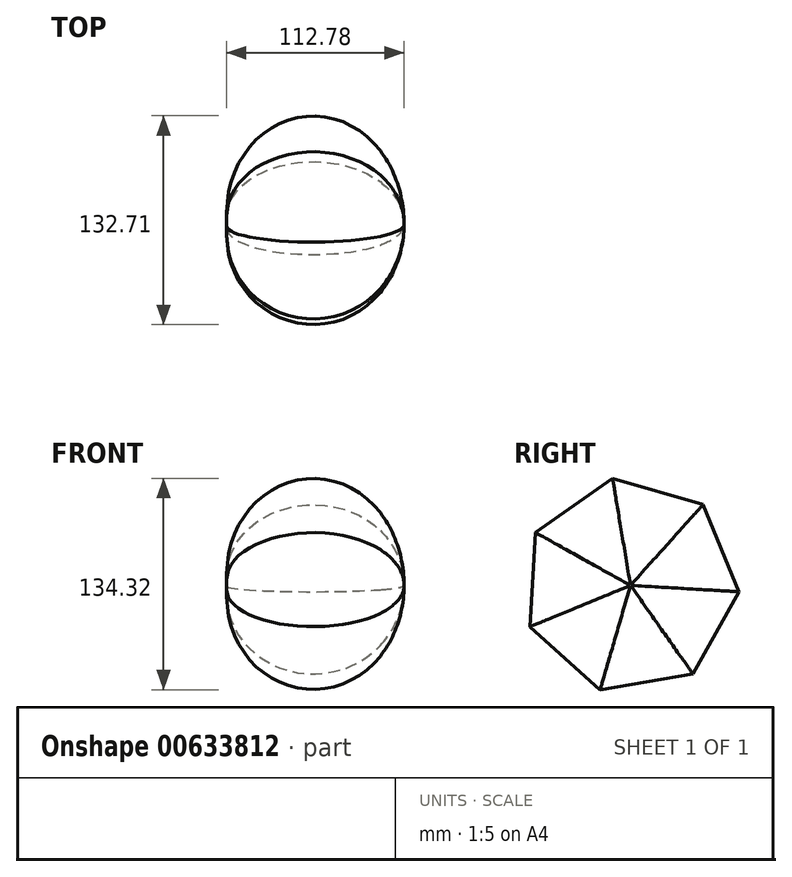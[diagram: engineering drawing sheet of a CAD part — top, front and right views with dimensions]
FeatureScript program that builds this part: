
annotation { "Feature Type Name" : "Feature", "Feature Type Description" : "" }
export const myFeature = defineFeature(function(context is Context, id is Id, definition is map)
    precondition{}
    {
        {
            var Q0;
            Q0=qCreatedBy(makeId("Right.planeOp"),FACE);
            var sketch = newSketch(context, id + "F0", { "sketchPlane" : qUnion([Q0])});
            skCircle(sketch, "E0", {"center": v(-0.1, 0.47) * mm, "radius": 76.2 * mm});
            skSolve(sketch);
        }
        {
            var Q0;
            Q0=makeQuery(id+"F0.imprint","IMPRINT",FACE,{"disambiguationData":[TD([[makeQuery(id+"F0.imprint","IMPRINT",EDGE,{"derivedFrom":sQuery(id+"F0.wireOp",EDGE,"E0")}),1.0]])]});
            var sketch = newSketch(context, id + "F1", { "sketchPlane" : qUnion([Q0])});
            skCircle(sketch, "E1.cCircle", {"center": v(0, 0) * mm, "radius": 65.95 * mm, "construction": true});
            skLineSegment(sketch, "E1.0", {"start": v(73.07, -4.29) * mm, "end": v(42.2, -59.8) * mm});
            skLineSegment(sketch, "E1.1", {"start": v(42.2, -59.8) * mm, "end": v(-20.44, -70.28) * mm});
            skLineSegment(sketch, "E1.2", {"start": v(-20.44, -70.28) * mm, "end": v(-67.7, -27.84) * mm});
            skLineSegment(sketch, "E1.3", {"start": v(-67.7, -27.84) * mm, "end": v(-63.97, 35.56) * mm});
            skLineSegment(sketch, "E1.4", {"start": v(-63.97, 35.56) * mm, "end": v(-12.08, 72.19) * mm});
            skLineSegment(sketch, "E1.5", {"start": v(-12.08, 72.19) * mm, "end": v(48.9, 54.46) * mm});
            skLineSegment(sketch, "E1.6", {"start": v(48.9, 54.46) * mm, "end": v(73.07, -4.29) * mm});
            skPoint(sketch, "E1.0.midPoint", {"position": v(57.64, -32.04) * mm});
            skSolve(sketch);
        }
        {
            var Q0;
            Q0 = qSketchRegion(id + "F1", true);
            extrude(context, id + "F2", {"entities" : qUnion([Q0]), "depth" : 112.78 * mm, "offsetDistance" : 25.4 * mm});
        }
        {
            var Q0;
            Q0=makeQuery(id+"F2.opExtrude","CAP_FACE",FACE,{"disambiguationData":[OSD([sQuery(id+"F1.wireOp",EDGE,"E1.0"),sQuery(id+"F1.wireOp",EDGE,"E1.1"),sQuery(id+"F1.wireOp",EDGE,"E1.2"),sQuery(id+"F1.wireOp",EDGE,"E1.3"),sQuery(id+"F1.wireOp",EDGE,"E1.4"),sQuery(id+"F1.wireOp",EDGE,"E1.5"),sQuery(id+"F1.wireOp",EDGE,"E1.6")])],"isStart":false});
            fillet(context, id + "F3", {"entities" : qUnion([Q0]), "radius" : 65.61 * mm, "tangentPropagation" : true, "allowEdgeOverflow" : false});
        }
        {
            var Q0;
            Q0=makeQuery(id+"F2.opExtrude","CAP_EDGE",EDGE,{"disambiguationData":[OSD([sQuery(id+"F1.wireOp",EDGE,"E1.3")])],"isStart":true});
            var Q1;
            Q1=makeQuery(id+"F2.opExtrude","CAP_EDGE",EDGE,{"disambiguationData":[OSD([sQuery(id+"F1.wireOp",EDGE,"E1.4")])],"isStart":true});
            var Q2;
            Q2=makeQuery(id+"F2.opExtrude","CAP_EDGE",EDGE,{"disambiguationData":[OSD([sQuery(id+"F1.wireOp",EDGE,"E1.5")])],"isStart":true});
            var Q3;
            Q3=makeQuery(id+"F2.opExtrude","CAP_EDGE",EDGE,{"disambiguationData":[OSD([sQuery(id+"F1.wireOp",EDGE,"E1.6")])],"isStart":true});
            var Q4;
            Q4=makeQuery(id+"F2.opExtrude","CAP_EDGE",EDGE,{"disambiguationData":[OSD([sQuery(id+"F1.wireOp",EDGE,"E1.0")])],"isStart":true});
            var Q5;
            Q5=makeQuery(id+"F2.opExtrude","CAP_EDGE",EDGE,{"disambiguationData":[OSD([sQuery(id+"F1.wireOp",EDGE,"E1.1")])],"isStart":true});
            var Q6;
            Q6=makeQuery(id+"F2.opExtrude","CAP_EDGE",EDGE,{"disambiguationData":[OSD([sQuery(id+"F1.wireOp",EDGE,"E1.2")])],"isStart":true});
            fillet(context, id + "F4", {"entities" : qUnion([Q0, Q1, Q2, Q3, Q4, Q5, Q6]), "radius" : 55.19 * mm, "tangentPropagation" : true, "allowEdgeOverflow" : false});
        }
    });
